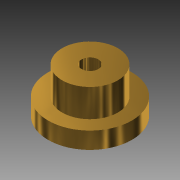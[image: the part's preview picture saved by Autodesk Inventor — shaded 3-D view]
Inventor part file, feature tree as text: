
AUTODESK INVENTOR PART (.ipt)
format: ipt  version: 2015 (Build 190159000, 159)  size: 112,128 bytes
history: native  units: mm
features: extrude x3, sketch x3, other x2
ambient origin geometry x8: Origin, YZ Plane, XZ Plane, XY Plane, X Axis, Y Axis, Z Axis, Center Point
bodies: Body1 (feature_tree)
feature tree (8):
  other  "Gear3_S50B 30B+0303"
  other  "ソリッド1"
  extrude  "押し出し1"  Depth=15.0mm
  extrude  "押し出し3"  Depth=3.0mm TaperAngle=0.0deg
  extrude  "押し出し4"  Depth=10.0mm
  sketch  "スケッチ1"
  sketch  "スケッチ3"
  sketch  "スケッチ4"
